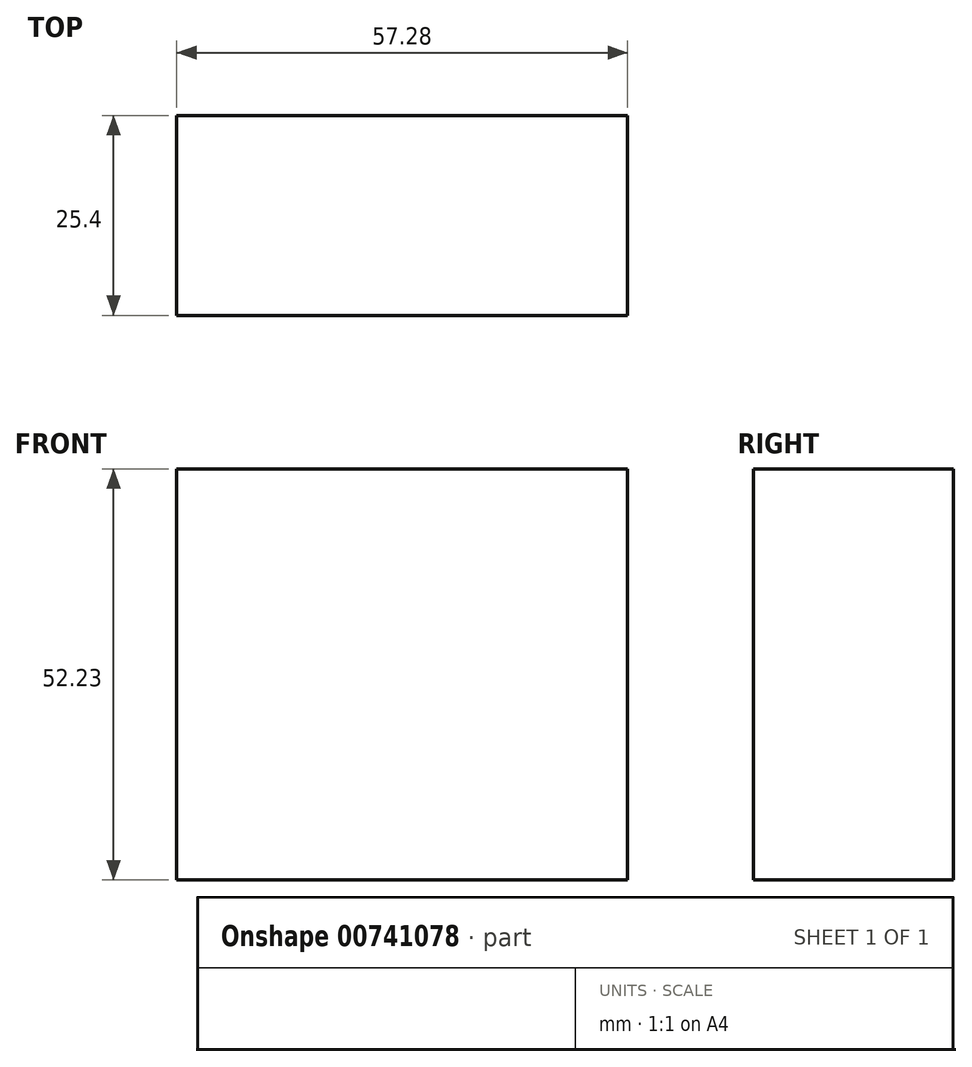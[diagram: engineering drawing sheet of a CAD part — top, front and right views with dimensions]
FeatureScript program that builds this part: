
annotation { "Feature Type Name" : "Feature", "Feature Type Description" : "" }
export const myFeature = defineFeature(function(context is Context, id is Id, definition is map)
    precondition{}
    {
        {
            var Q0;
            Q0=qCreatedBy(makeId("Front.planeOp"),FACE);
            var sketch = newSketch(context, id + "F0", { "sketchPlane" : qUnion([Q0])});
            skLineSegment(sketch, "E0.bottom", {"start": v(0, 0) * mm, "end": v(-57.28, 0) * mm});
            skLineSegment(sketch, "E0.top", {"start": v(0, 52.23) * mm, "end": v(-57.28, 52.23) * mm});
            skLineSegment(sketch, "E0.left", {"start": v(0, 0) * mm, "end": v(0, 52.23) * mm});
            skLineSegment(sketch, "E0.right", {"start": v(-57.28, 0) * mm, "end": v(-57.28, 52.23) * mm});
            skSolve(sketch);
        }
        {
            var Q0;
            Q0=makeQuery(id+"F0.imprint","IMPRINT",FACE,{"disambiguationData":[TD([[makeQuery(id+"F0.imprint","IMPRINT",EDGE,{"derivedFrom":sQuery(id+"F0.wireOp",EDGE,"E0.bottom")}),-1.0]])]});
            extrude(context, id + "F1", {"entities" : qUnion([Q0]), "depth" : 25.4 * mm, "offsetDistance" : 25.4 * mm});
        }
    });
